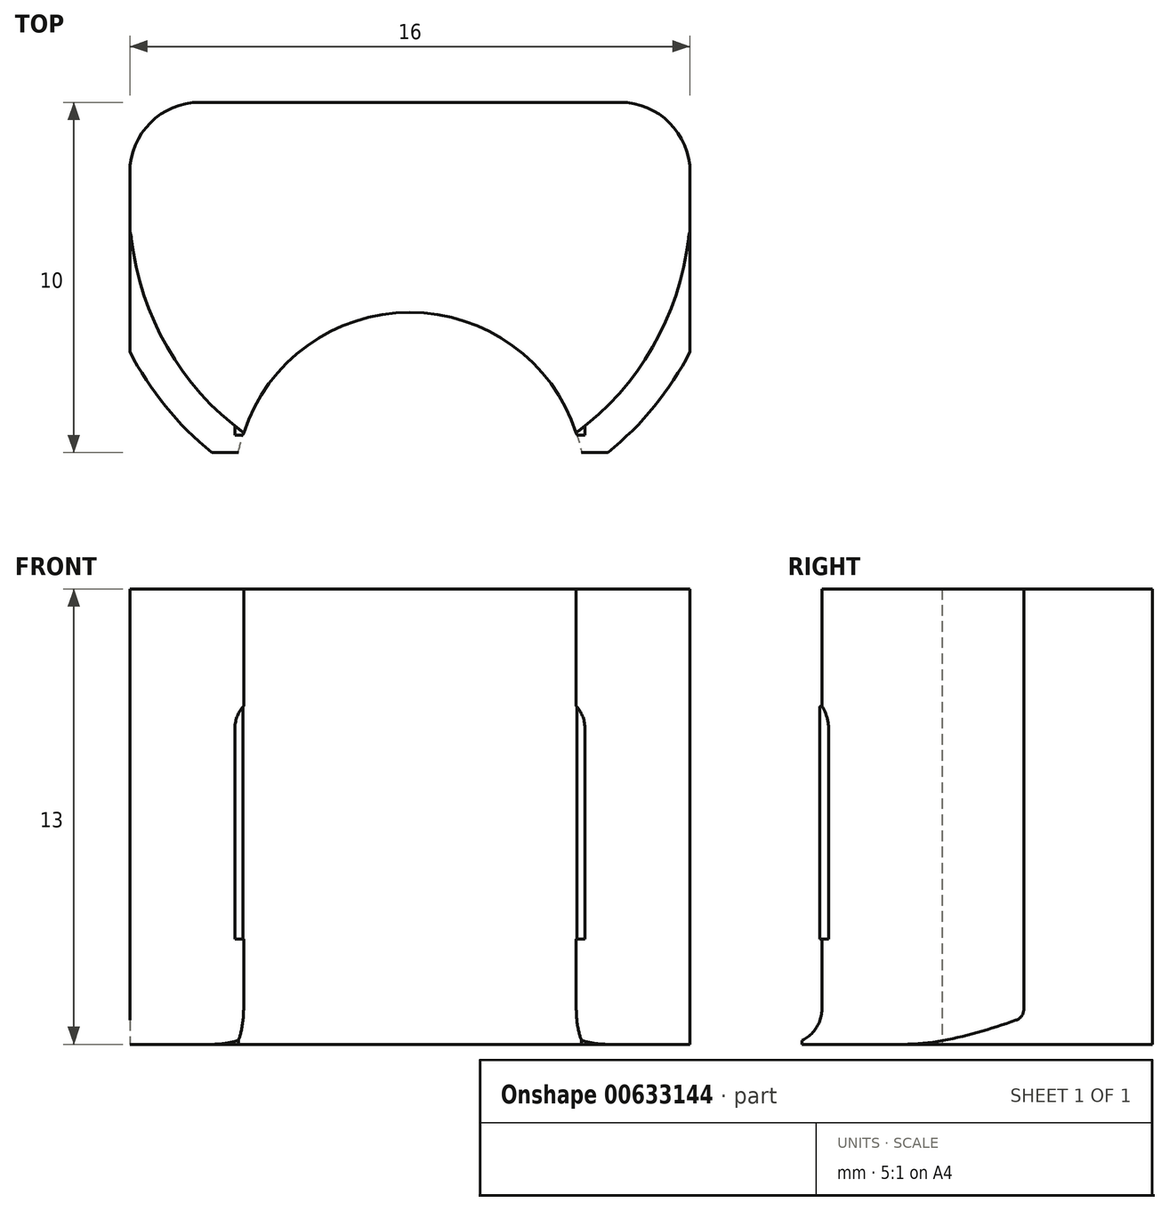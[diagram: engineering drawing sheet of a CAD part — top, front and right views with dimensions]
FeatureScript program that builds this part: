
annotation { "Feature Type Name" : "Feature", "Feature Type Description" : "" }
export const myFeature = defineFeature(function(context is Context, id is Id, definition is map)
    precondition{}
    {
        {
            var Q0;
            Q0=qCreatedBy(makeId("Front.planeOp"),FACE);
            var sketch = newSketch(context, id + "F0", { "sketchPlane" : qUnion([Q0])});
            skLineSegment(sketch, "E0", {"start": v(0, 0) * mm, "end": v(0, 10) * mm});
            skLineSegment(sketch, "E1", {"start": v(0, 10) * mm, "end": v(5, 10) * mm});
            skLineSegment(sketch, "E2", {"start": v(5, 10) * mm, "end": v(5, 0) * mm});
            skLineSegment(sketch, "E3", {"start": v(5, 0) * mm, "end": v(8, 0) * mm});
            skLineSegment(sketch, "E4", {"start": v(8, 0) * mm, "end": v(8, 13) * mm});
            skLineSegment(sketch, "E5", {"start": v(8, 13) * mm, "end": v(0, 13) * mm});
            skLineSegment(sketch, "E6", {"start": v(0, 13) * mm, "end": v(0, 10) * mm});
            skSolve(sketch);
        }
        {
            var Q0;
            Q0=qSketchRegion(id+"F0",true);
            extrude(context, id + "F1", {"entities" : qUnion([Q0]), "endBound" : BoundingType.SYMMETRIC, "depth" : 12 * mm, "offsetDistance" : 25 * mm});
        }
        {
            var Q0;
            Q0=qCreatedBy(makeId("Top.planeOp"),FACE);
            var sketch = newSketch(context, id + "F2", { "sketchPlane" : qUnion([Q0])});
            skLineSegment(sketch, "E7", {"start": v(0, 0) * mm, "end": v(8, 0) * mm});
            skLineSegment(sketch, "E8", {"start": v(8, 0) * mm, "end": v(8, 14) * mm, "construction": true});
            skLineSegment(sketch, "E9", {"start": v(8, 14) * mm, "end": v(11, 14) * mm});
            skLineSegment(sketch, "E10", {"start": v(11, 14) * mm, "end": v(8, 0) * mm});
            skArc(sketch, "E11", {"start": v(0, 6) * mm, "mid": v(5.66, 8.34) * mm, "end": v(8, 14) * mm});
            skLineSegment(sketch, "E12", {"start": v(0, 6) * mm, "end": v(0, 0) * mm});
            skSolve(sketch);
        }
        {
            var Q0;
            Q0=makeQuery(id+"F2.imprint","IMPRINT",FACE,{"disambiguationData":[TD([[makeQuery(id+"F2.imprint","IMPRINT",EDGE,{"derivedFrom":sQuery(id+"F2.wireOp",EDGE,"E7")}),1.0]])]});
            extrude(context, id + "F3", {"entities" : qUnion([Q0]), "depth" : 13 * mm, "offsetDistance" : 25 * mm});
        }
        {
            var Q0;
            Q0=makeQuery(id+"F3.opExtrude","SWEPT_BODY",BODY,{"disambiguationData":[OSD([sQuery(id+"F2.wireOp",EDGE,"E7"),sQuery(id+"F2.wireOp",EDGE,"E9"),sQuery(id+"F2.wireOp",EDGE,"E10"),sQuery(id+"F2.wireOp",EDGE,"E11"),sQuery(id+"F2.wireOp",EDGE,"E12")])]});
            transform(context, id + "F4", {"entities" : qUnion([Q0]), "transformType" : TransformType.TRANSLATION_3D, "dx" : 0 * mm, "dy" : 0 * mm, "dz" : 0 * mm, "makeCopy" : false});
        }
        {
            var Q0;
            Q0=qCreatedBy(makeId("Front.planeOp"),FACE);
            var sketch = newSketch(context, id + "F5", { "sketchPlane" : qUnion([Q0])});
            skLineSegment(sketch, "E13.top", {"start": v(0, 10) * mm, "end": v(5, 10) * mm});
            skLineSegment(sketch, "E13.left", {"start": v(0, 0) * mm, "end": v(0, 10) * mm});
            skLineSegment(sketch, "E13.right", {"start": v(5, 0) * mm, "end": v(5, 10) * mm});
            skLineSegment(sketch, "E14", {"start": v(0, 0) * mm, "end": v(0, 3) * mm});
            skLineSegment(sketch, "E15", {"start": v(0, 3) * mm, "end": v(5, 3) * mm});
            skSolve(sketch);
        }
        {
            var Q0;
            Q0=qSketchRegion(id+"F5",true);
            extrude(context, id + "F6", {"entities" : qUnion([Q0]), "endBound" : BoundingType.SYMMETRIC, "depth" : 25 * mm, "offsetDistance" : 25 * mm});
        }
        {
            var Q0;
            Q0=makeQuery(id+"F6.opExtrude","SWEPT_BODY",BODY,{"disambiguationData":[OSD([sQuery(id+"F5.wireOp",EDGE,"E13.bottom"),sQuery(id+"F5.wireOp",EDGE,"E13.top"),sQuery(id+"F5.wireOp",EDGE,"E13.left"),sQuery(id+"F5.wireOp",EDGE,"E13.right")])]});
            var Q1;
            Q1=makeQuery(id+"F3.opExtrude","SWEPT_BODY",BODY,{"disambiguationData":[OSD([sQuery(id+"F2.wireOp",EDGE,"E7"),sQuery(id+"F2.wireOp",EDGE,"E9"),sQuery(id+"F2.wireOp",EDGE,"E10"),sQuery(id+"F2.wireOp",EDGE,"E11"),sQuery(id+"F2.wireOp",EDGE,"E12")])]});
            booleanBodies(context, id + "F7", {"operationType" : BooleanOperationType.SUBTRACTION, "tools" : qUnion([Q0]), "targets" : qUnion([Q1])});
        }
        {
            var Q0;
            Q0=qCreatedBy(makeId("Right.planeOp"),FACE);
            var sketch = newSketch(context, id + "F8", { "sketchPlane" : qUnion([Q0])});
            skLineSegment(sketch, "E16", {"start": v(0, 0) * mm, "end": v(0, 9) * mm});
            skLineSegment(sketch, "E17", {"start": v(0, 9) * mm, "end": v(7.5, 9) * mm});
            skLineSegment(sketch, "E18", {"start": v(7.5, 9) * mm, "end": v(7.5, 4) * mm});
            skLineSegment(sketch, "E19", {"start": v(7.5, 4) * mm, "end": v(6, 4) * mm});
            skLineSegment(sketch, "E20", {"start": v(6, 4) * mm, "end": v(6, 9) * mm});
            skSolve(sketch);
        }
        {
            var Q0;
            {var subQ0=sQuery(id+"F8.wireOp",EDGE,"E18");Q0=makeQuery(id+"F8.imprint","IMPRINT",FACE,{"disambiguationData":[TD([[makeQuery(id+"F8.imprint","IMPRINT",EDGE,{"derivedFrom":subQ0}),-1.0]])]});}
            extrude(context, id + "F9", {"entities" : qUnion([Q0]), "depth" : 25 * mm, "offsetDistance" : 25 * mm});
        }
        {
            var Q0;
            Q0=makeQuery(id+"F9.opExtrude","SWEPT_BODY",BODY,{"disambiguationData":[OSD([sQuery(id+"F8.wireOp",EDGE,"E17"),sQuery(id+"F8.wireOp",EDGE,"E18"),sQuery(id+"F8.wireOp",EDGE,"E19"),sQuery(id+"F8.wireOp",EDGE,"E20")])]});
            var Q1;
            Q1=makeQuery(id+"F3.opExtrude","SWEPT_BODY",BODY,{"disambiguationData":[OSD([sQuery(id+"F2.wireOp",EDGE,"E7"),sQuery(id+"F2.wireOp",EDGE,"E9"),sQuery(id+"F2.wireOp",EDGE,"E10"),sQuery(id+"F2.wireOp",EDGE,"E11"),sQuery(id+"F2.wireOp",EDGE,"E12")])]});
            booleanBodies(context, id + "F10", {"operationType" : BooleanOperationType.SUBTRACTION, "tools" : qUnion([Q0]), "targets" : qUnion([Q1])});
        }
        {
            var Q0;
            Q0=qCreatedBy(makeId("Top.planeOp"),FACE);
            var sketch = newSketch(context, id + "F11", { "sketchPlane" : qUnion([Q0])});
            skLineSegment(sketch, "E21", {"start": v(0, 0) * mm, "end": v(5, 0) * mm});
            skLineSegment(sketch, "E22", {"start": v(5, 0) * mm, "end": v(5, 5) * mm});
            skLineSegment(sketch, "E23", {"start": v(5, 5) * mm, "end": v(0, 5) * mm});
            skLineSegment(sketch, "E24", {"start": v(0, 5) * mm, "end": v(0, 0) * mm});
            skSolve(sketch);
        }
        {
            var Q0;
            Q0=qSketchRegion(id+"F11",true);
            extrude(context, id + "F12", {"entities" : qUnion([Q0]), "endBound" : BoundingType.SYMMETRIC, "depth" : 8 * mm, "offsetDistance" : 25 * mm});
        }
        {
            var Q0;
            Q0=makeQuery(id+"F12.opExtrude","SWEPT_BODY",BODY,{"disambiguationData":[OSD([sQuery(id+"F11.wireOp",EDGE,"E21"),sQuery(id+"F11.wireOp",EDGE,"E22"),sQuery(id+"F11.wireOp",EDGE,"E23"),sQuery(id+"F11.wireOp",EDGE,"E24")])]});
            var Q1;
            Q1=makeQuery(id+"F3.opExtrude","SWEPT_BODY",BODY,{"disambiguationData":[OSD([sQuery(id+"F2.wireOp",EDGE,"E7"),sQuery(id+"F2.wireOp",EDGE,"E9"),sQuery(id+"F2.wireOp",EDGE,"E10"),sQuery(id+"F2.wireOp",EDGE,"E11"),sQuery(id+"F2.wireOp",EDGE,"E12")])]});
            booleanBodies(context, id + "F13", {"operationType" : BooleanOperationType.SUBTRACTION, "tools" : qUnion([Q0]), "targets" : qUnion([Q1])});
        }
        {
            var Q0;
            Q0=makeQuery(id+"F1.opExtrude","SWEPT_BODY",BODY,{"disambiguationData":[OSD([sQuery(id+"F0.wireOp",EDGE,"E1"),sQuery(id+"F0.wireOp",EDGE,"E2"),sQuery(id+"F0.wireOp",EDGE,"E3"),sQuery(id+"F0.wireOp",EDGE,"E4"),sQuery(id+"F0.wireOp",EDGE,"E5"),sQuery(id+"F0.wireOp",EDGE,"E6")])]});
            var Q1;
            Q1=makeQuery(id+"F3.opExtrude","SWEPT_BODY",BODY,{"disambiguationData":[OSD([sQuery(id+"F2.wireOp",EDGE,"E7"),sQuery(id+"F2.wireOp",EDGE,"E9"),sQuery(id+"F2.wireOp",EDGE,"E10"),sQuery(id+"F2.wireOp",EDGE,"E11"),sQuery(id+"F2.wireOp",EDGE,"E12")])]});
            booleanBodies(context, id + "F14", {"operationType" : BooleanOperationType.UNION, "tools" : qUnion([Q0, Q1])});
        }
        {
            var Q0;
            Q0=makeQuery(id+"F3.opExtrude","SWEPT_EDGE",EDGE,{"disambiguationData":[OSD([sQuery(id+"F2.wireOp",EDGE,"E9"),sQuery(id+"F2.wireOp",EDGE,"E10")])]});
            var Q1;
            Q1=makeQuery(id+"F3.opExtrude","SWEPT_EDGE",EDGE,{"disambiguationData":[OSD([sQuery(id+"F2.wireOp",EDGE,"E9"),sQuery(id+"F2.wireOp",EDGE,"E11")])]});
            var Q2;
            Q2=makeQuery(id+"F7.opBoolean","COPY",EDGE,{"derivedFrom":makeQuery(id+"F6.opExtrude","SWEPT_EDGE",EDGE,{"disambiguationData":[OSD([sQuery(id+"F5.wireOp",EDGE,"E13.right"),sQuery(id+"F5.wireOp",EDGE,"E15")])]})});
            var Q3;
            Q3=makeQuery(id+"F14.opBoolean","MERGE",EDGE,{"derivedFrom":[makeQuery(id+"F1.opExtrude","SWEPT_EDGE",EDGE,{"disambiguationData":[OSD([sQuery(id+"F0.wireOp",EDGE,"E1"),sQuery(id+"F0.wireOp",EDGE,"E2")])]}),makeQuery(id+"F7.opBoolean","COPY",EDGE,{"derivedFrom":makeQuery(id+"F6.opExtrude","SWEPT_EDGE",EDGE,{"disambiguationData":[OSD([sQuery(id+"F5.wireOp",EDGE,"E13.top"),sQuery(id+"F5.wireOp",EDGE,"E13.right")])]})})]});
            var Q4;
            Q4=makeQuery(id+"F1.opExtrude","SWEPT_EDGE",EDGE,{"disambiguationData":[OSD([sQuery(id+"F0.wireOp",EDGE,"E2"),sQuery(id+"F0.wireOp",EDGE,"E3")])]});
            var Q5;
            Q5=makeQuery(id+"F13.opBoolean","INTERSECT",EDGE,{"derivedFrom":[makeQuery(id+"F3.opExtrude","CAP_FACE",FACE,{"disambiguationData":[OSD([sQuery(id+"F2.wireOp",EDGE,"E7"),sQuery(id+"F2.wireOp",EDGE,"E9"),sQuery(id+"F2.wireOp",EDGE,"E10"),sQuery(id+"F2.wireOp",EDGE,"E11"),sQuery(id+"F2.wireOp",EDGE,"E12")])],"isStart":true}),makeQuery(id+"F12.opExtrude","SWEPT_FACE",FACE,{"disambiguationData":[OSD([sQuery(id+"F11.wireOp",EDGE,"E23")])]})]});
            var Q6;
            Q6=makeQuery(id+"F3.opExtrude","CAP_EDGE",EDGE,{"disambiguationData":[OSD([sQuery(id+"F2.wireOp",EDGE,"E11")])],"isStart":true});
            var Q7;
            Q7=makeQuery(id+"F3.opExtrude","CAP_EDGE",EDGE,{"disambiguationData":[OSD([sQuery(id+"F2.wireOp",EDGE,"E10")])],"isStart":true});
            var Q8;
            Q8=makeQuery(id+"F1.opExtrude","SWEPT_EDGE",EDGE,{"disambiguationData":[OSD([sQuery(id+"F0.wireOp",EDGE,"E3"),sQuery(id+"F0.wireOp",EDGE,"E4")])]});
            var Q9;
            Q9=makeQuery(id+"F3.opExtrude","CAP_EDGE",EDGE,{"disambiguationData":[OSD([sQuery(id+"F2.wireOp",EDGE,"E9")])],"isStart":true});
            fillet(context, id + "F15", {"entities" : qUnion([Q0, Q1, Q2, Q3, Q4, Q5, Q6, Q7, Q8, Q9]), "radius" : 1 * mm, "tangentPropagation" : true, "allowEdgeOverflow" : false});
        }
        {
            var Q0;
            Q0=makeQuery(id+"F1.opExtrude","SWEPT_BODY",BODY,{"disambiguationData":[OSD([sQuery(id+"F0.wireOp",EDGE,"E1"),sQuery(id+"F0.wireOp",EDGE,"E2"),sQuery(id+"F0.wireOp",EDGE,"E3"),sQuery(id+"F0.wireOp",EDGE,"E4"),sQuery(id+"F0.wireOp",EDGE,"E5"),sQuery(id+"F0.wireOp",EDGE,"E6")])]});
            var Q1;
            Q1=qCreatedBy(makeId("Right.planeOp"),FACE);
            mirror(context, id + "F16", {"operationType" : NewBodyOperationType.ADD, "entities" : qUnion([Q0]), "mirrorPlane" : qUnion([Q1])});
        }
        {
            var Q0;
            Q0=qCreatedBy(makeId("Top.planeOp"),FACE);
            var sketch = newSketch(context, id + "F17", { "sketchPlane" : qUnion([Q0])});
            skLineSegment(sketch, "E25", {"start": v(0, 0) * mm, "end": v(0, 14) * mm});
            skLineSegment(sketch, "E26", {"start": v(0, 14) * mm, "end": v(-8, 14) * mm});
            skLineSegment(sketch, "E27", {"start": v(-8, 14) * mm, "end": v(-8, 17) * mm});
            skLineSegment(sketch, "E28", {"start": v(-8, 17) * mm, "end": v(8, 17) * mm});
            skLineSegment(sketch, "E29", {"start": v(8, 17) * mm, "end": v(8, 7) * mm});
            skLineSegment(sketch, "E30", {"start": v(8, 7) * mm, "end": v(-8, 7) * mm});
            skLineSegment(sketch, "E31", {"start": v(-8, 7) * mm, "end": v(-8, 14) * mm});
            skSolve(sketch);
        }
        {
            var Q0;
            Q0 = qSketchRegion(id + "F17", true);
            extrude(context, id + "F18", {"entities" : qUnion([Q0]), "depth" : 13 * mm, "offsetDistance" : 25 * mm});
        }
        {
            var Q0;
            Q0=qCreatedBy(makeId("Top.planeOp"),FACE);
            var sketch = newSketch(context, id + "F19", { "sketchPlane" : qUnion([Q0])});
            skLineSegment(sketch, "E32", {"start": v(0, 0) * mm, "end": v(0, 6) * mm});
            skCircle(sketch, "E33", {"center": v(0, 6) * mm, "radius": 5 * mm});
            skSolve(sketch);
        }
        {
            var Q0;
            Q0 = qSketchRegion(id + "F19", true);
            extrude(context, id + "F20", {"entities" : qUnion([Q0]), "depth" : 25 * mm, "offsetDistance" : 25 * mm});
        }
        {
            var Q0;
            Q0=makeQuery(id+"F20.opExtrude","SWEPT_BODY",BODY,{"disambiguationData":[OSD([sQuery(id+"F19.wireOp",EDGE,"E33")])]});
            var Q1;
            Q1=makeQuery(id+"F18.opExtrude","SWEPT_BODY",BODY,{"disambiguationData":[OSD([sQuery(id+"F17.wireOp",EDGE,"E27"),sQuery(id+"F17.wireOp",EDGE,"E28"),sQuery(id+"F17.wireOp",EDGE,"E29"),sQuery(id+"F17.wireOp",EDGE,"E30"),sQuery(id+"F17.wireOp",EDGE,"E31")])]});
            booleanBodies(context, id + "F21", {"operationType" : BooleanOperationType.SUBTRACTION, "tools" : qUnion([Q0]), "targets" : qUnion([Q1])});
        }
        {
            var Q0;
            Q0=qCreatedBy(makeId("Right.planeOp"),FACE);
            var sketch = newSketch(context, id + "F22", { "sketchPlane" : qUnion([Q0])});
            skLineSegment(sketch, "E34", {"start": v(0, 0) * mm, "end": v(0, 4) * mm});
            skLineSegment(sketch, "E35", {"start": v(0, 4) * mm, "end": v(6, 4) * mm});
            skLineSegment(sketch, "E36", {"start": v(6, 4) * mm, "end": v(6, 11) * mm});
            skLineSegment(sketch, "E37", {"start": v(6, 11) * mm, "end": v(7.5, 11) * mm});
            skLineSegment(sketch, "E38", {"start": v(7.5, 11) * mm, "end": v(7.5, 2) * mm});
            skLineSegment(sketch, "E39", {"start": v(7.5, 2) * mm, "end": v(6, 2) * mm});
            skLineSegment(sketch, "E40", {"start": v(6, 2) * mm, "end": v(6, 4) * mm});
            skSolve(sketch);
        }
        {
            var Q0;
            Q0 = qSketchRegion(id + "F22", true);
            extrude(context, id + "F23", {"entities" : qUnion([Q0]), "endBound" : BoundingType.SYMMETRIC, "depth" : 25 * mm, "offsetDistance" : 25 * mm});
        }
        {
            var Q0;
            Q0=makeQuery(id+"F23.opExtrude","SWEPT_BODY",BODY,{"disambiguationData":[OSD([sQuery(id+"F22.wireOp",EDGE,"E36"),sQuery(id+"F22.wireOp",EDGE,"E37"),sQuery(id+"F22.wireOp",EDGE,"5Y3vSUpP-A0kN-DOeO-62DO-3T6u22OxACCr"),sQuery(id+"F22.wireOp",EDGE,"PLsNgynX-nngj-ABZZ-APAf-ubLvABKjYrFa")])]});
            var Q1;
            Q1=makeQuery(id+"F18.opExtrude","SWEPT_BODY",BODY,{"disambiguationData":[OSD([sQuery(id+"F17.wireOp",EDGE,"E27"),sQuery(id+"F17.wireOp",EDGE,"E28"),sQuery(id+"F17.wireOp",EDGE,"E29"),sQuery(id+"F17.wireOp",EDGE,"E30"),sQuery(id+"F17.wireOp",EDGE,"E31")])]});
            booleanBodies(context, id + "F24", {"operationType" : BooleanOperationType.SUBTRACTION, "tools" : qUnion([Q0]), "targets" : qUnion([Q1])});
        }
        {
            var Q0;
            Q0=makeQuery(id+"F1.opExtrude","SWEPT_BODY",BODY,{"disambiguationData":[OSD([sQuery(id+"F0.wireOp",EDGE,"E1"),sQuery(id+"F0.wireOp",EDGE,"E2"),sQuery(id+"F0.wireOp",EDGE,"E3"),sQuery(id+"F0.wireOp",EDGE,"E4"),sQuery(id+"F0.wireOp",EDGE,"E5"),sQuery(id+"F0.wireOp",EDGE,"E6")])]});
            var Q1;
            Q1=makeQuery(id+"F18.opExtrude","SWEPT_BODY",BODY,{"disambiguationData":[OSD([sQuery(id+"F17.wireOp",EDGE,"E27"),sQuery(id+"F17.wireOp",EDGE,"E28"),sQuery(id+"F17.wireOp",EDGE,"E29"),sQuery(id+"F17.wireOp",EDGE,"E30"),sQuery(id+"F17.wireOp",EDGE,"E31")])]});
            booleanBodies(context, id + "F25", {"operationType" : BooleanOperationType.SUBTRACTION, "tools" : qUnion([Q0]), "targets" : qUnion([Q1]), "keepTools" : true});
        }
        {
            var Q0;
            Q0=makeQuery(id+"F18.opExtrude","SWEPT_EDGE",EDGE,{"disambiguationData":[OSD([sQuery(id+"F17.wireOp",EDGE,"E28"),sQuery(id+"F17.wireOp",EDGE,"E29")])]});
            var Q1;
            Q1=makeQuery(id+"F18.opExtrude","SWEPT_EDGE",EDGE,{"disambiguationData":[OSD([sQuery(id+"F17.wireOp",EDGE,"E27"),sQuery(id+"F17.wireOp",EDGE,"E28")])]});
            fillet(context, id + "F26", {"entities" : qUnion([Q0, Q1]), "radius" : 2 * mm, "tangentPropagation" : true, "allowEdgeOverflow" : false});
        }
        {
            var Q0;
            Q0=makeQuery(id+"F1.opExtrude","SWEPT_BODY",BODY,{"disambiguationData":[OSD([sQuery(id+"F0.wireOp",EDGE,"E1"),sQuery(id+"F0.wireOp",EDGE,"E2"),sQuery(id+"F0.wireOp",EDGE,"E3"),sQuery(id+"F0.wireOp",EDGE,"E4"),sQuery(id+"F0.wireOp",EDGE,"E5"),sQuery(id+"F0.wireOp",EDGE,"E6")])]});
            deleteBodies(context, id + "F27", {"entities" : qUnion([Q0])});
        }
    });
